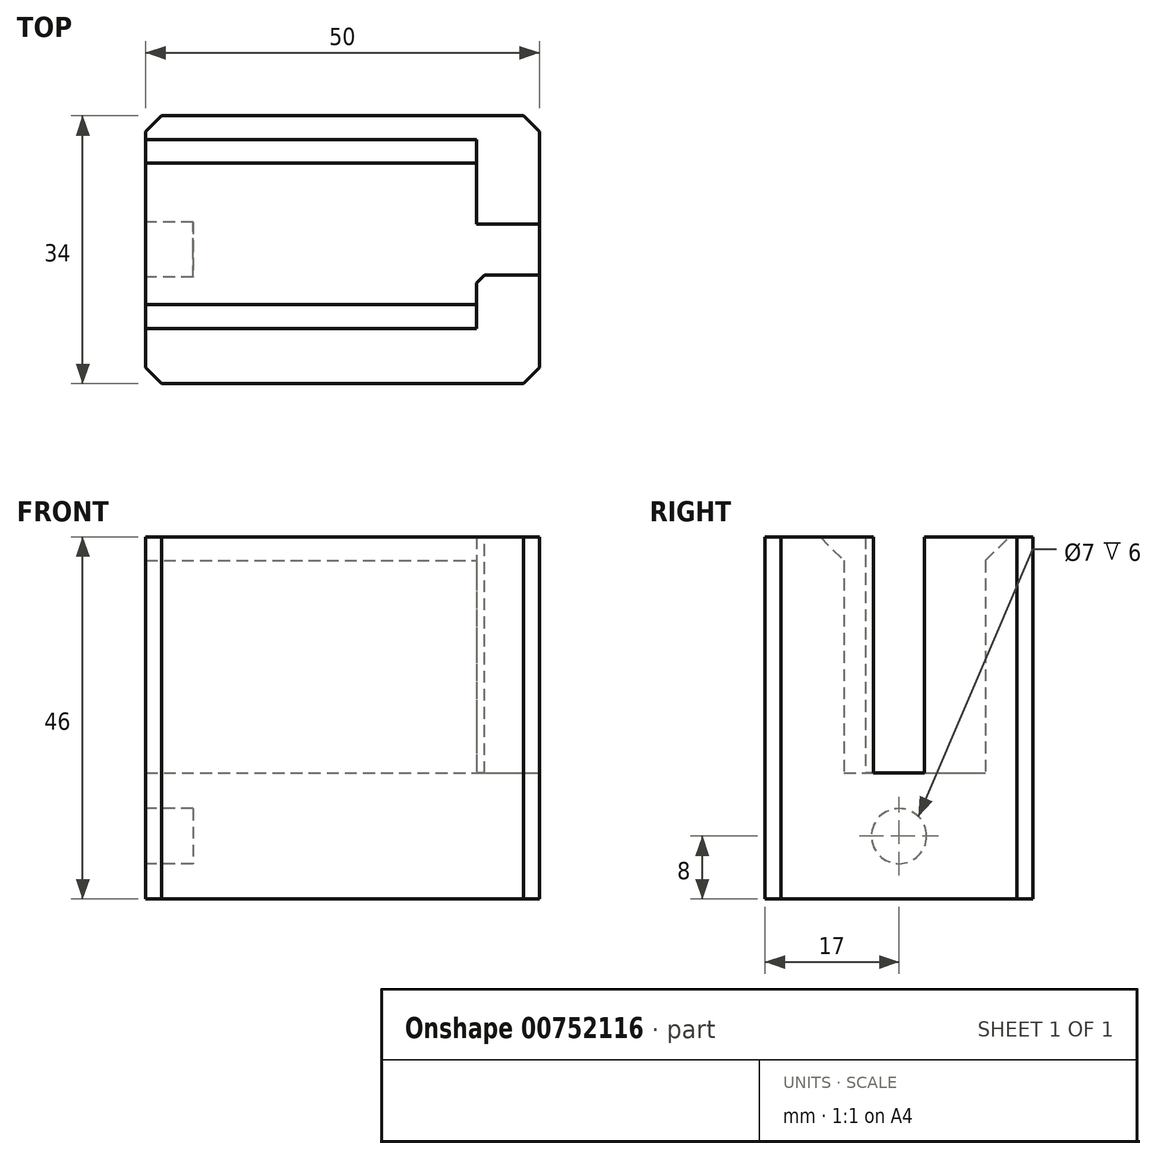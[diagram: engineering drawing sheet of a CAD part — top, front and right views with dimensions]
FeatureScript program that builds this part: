
annotation { "Feature Type Name" : "Feature", "Feature Type Description" : "" }
export const myFeature = defineFeature(function(context is Context, id is Id, definition is map)
    precondition{}
    {
        {
            var Q0;
            Q0=qCreatedBy(makeId("Front.planeOp"),FACE);
            var sketch = newSketch(context, id + "F0", { "sketchPlane" : qUnion([Q0])});
            skLineSegment(sketch, "E0.bottom", {"start": v(-25, 8) * mm, "end": v(-20, 8) * mm});
            skLineSegment(sketch, "E0.top", {"start": v(-25, -8) * mm, "end": v(25, -8) * mm});
            skLineSegment(sketch, "E0.left", {"start": v(-25, 8) * mm, "end": v(-25, -8) * mm});
            skLineSegment(sketch, "E0.right", {"start": v(25, 38) * mm, "end": v(25, -8) * mm});
            skPoint(sketch, "E0.middle", {"position": v(0, 0) * mm});
            skLineSegment(sketch, "E1.0", {"start": v(-20, 8) * mm, "end": v(-20, 8) * mm});
            skLineSegment(sketch, "E2.0", {"start": v(-20, 8) * mm, "end": v(17, 8) * mm});
            skLineSegment(sketch, "E3.0", {"start": v(17, 38) * mm, "end": v(17, 8) * mm});
            skPoint(sketch, "E4.orphan", {"position": v(25, 8) * mm});
            skLineSegment(sketch, "E5.trimOffspring", {"start": v(17, 38) * mm, "end": v(25, 38) * mm});
            skSolve(sketch);
        }
        {
            var Q0;
            Q0=qSketchRegion(id+"F0",true);
            extrude(context, id + "F1", {"entities" : qUnion([Q0]), "depth" : 34 * mm, "offsetDistance" : 25 * mm});
        }
        {
            var Q0;
            Q0=makeQuery(id+"F1.opExtrude","SWEPT_FACE",FACE,{"disambiguationData":[OSD([sQuery(id+"F0.wireOp",EDGE,"E0.right")])]});
            var sketch = newSketch(context, id + "F2", { "sketchPlane" : qUnion([Q0])});
            skLineSegment(sketch, "E6.bottom", {"start": v(-20.25, 38) * mm, "end": v(-13.75, 38) * mm});
            skLineSegment(sketch, "E6.top", {"start": v(-20.25, 8) * mm, "end": v(-13.75, 8) * mm});
            skLineSegment(sketch, "E6.left", {"start": v(-20.25, 38) * mm, "end": v(-20.25, 8) * mm});
            skLineSegment(sketch, "E6.right", {"start": v(-13.75, 38) * mm, "end": v(-13.75, 8) * mm});
            skSolve(sketch);
        }
        {
            var Q0;
            Q0=qSketchRegion(id+"F2",true);
            var Q1;
            Q1=makeQuery(id+"F1.opExtrude","SWEPT_FACE",FACE,{"disambiguationData":[OSD([sQuery(id+"F0.wireOp",EDGE,"E3.0")])]});
            extrude(context, id + "F3", {"entities" : qUnion([Q0]), "operationType" : NewBodyOperationType.REMOVE, "endBound" : BoundingType.UP_TO_SURFACE, "oppositeDirection" : true, "depth" : 25 * mm, "endBoundEntityFace" : qUnion([Q1]), "offsetDistance" : 25 * mm});
        }
        {
            var Q0;
            Q0=makeQuery(id+"F1.opExtrude","SWEPT_FACE",FACE,{"disambiguationData":[OSD([sQuery(id+"F0.wireOp",EDGE,"E0.left")])]});
            var sketch = newSketch(context, id + "F4", { "sketchPlane" : qUnion([Q0])});
            skCircle(sketch, "E7", {"center": v(17, 0) * mm, "radius": 3.5 * mm});
            skSolve(sketch);
        }
        {
            var Q0;
            Q0=qSketchRegion(id+"F4",true);
            extrude(context, id + "F5", {"entities" : qUnion([Q0]), "operationType" : NewBodyOperationType.REMOVE, "oppositeDirection" : true, "depth" : 6 * mm, "offsetDistance" : 25 * mm});
        }
        {
            var Q0;
            Q0=makeQuery(id+"F3.boolean.opBoolean","MERGE",FACE,{"derivedFrom":[makeQuery(id+"F1.opExtrude","SWEPT_FACE",FACE,{"disambiguationData":[OSD([sQuery(id+"F0.wireOp",EDGE,"E0.bottom"),sQuery(id+"F0.wireOp",EDGE,"E2.0")])]})],"fromTools":[makeQuery(id+"F3.opExtrude","SWEPT_FACE",FACE,{"disambiguationData":[OSD([sQuery(id+"F2.wireOp",EDGE,"E6.top")])]})]});
            var sketch = newSketch(context, id + "F6", { "sketchPlane" : qUnion([Q0])});
            skLineSegment(sketch, "E8.bottom", {"start": v(-25, -34) * mm, "end": v(17, -34) * mm});
            skLineSegment(sketch, "E8.top", {"start": v(-25, -24) * mm, "end": v(17, -24) * mm});
            skLineSegment(sketch, "E8.left", {"start": v(-25, -34) * mm, "end": v(-25, -24) * mm});
            skLineSegment(sketch, "E8.right", {"start": v(17, -34) * mm, "end": v(17, -24) * mm});
            skLineSegment(sketch, "E9.bottom", {"start": v(-25, 0) * mm, "end": v(17, 0) * mm});
            skLineSegment(sketch, "E9.top", {"start": v(-25, -6) * mm, "end": v(17, -6) * mm});
            skLineSegment(sketch, "E9.left", {"start": v(-25, 0) * mm, "end": v(-25, -6) * mm});
            skLineSegment(sketch, "E9.right", {"start": v(17, 0) * mm, "end": v(17, -6) * mm});
            skSolve(sketch);
        }
        {
            var Q0;
            Q0 = qSketchRegion(id + "F6", true);
            var Q1;
            {var subQ0=sQuery(id+"F0.wireOp",EDGE,"E5.trimOffspring");Q1=makeQuery(id+"F3.boolean.opBoolean","SPLIT",FACE,{"disambiguationData":[TD([makeQuery(id+"F3.opExtrude","SWEPT_FACE",FACE,{"disambiguationData":[OSD([sQuery(id+"F2.wireOp",EDGE,"E6.left")])]})])],"derivedFrom":makeQuery(id+"F1.opExtrude","SWEPT_FACE",FACE,{"disambiguationData":[OSD([subQ0])]})});}
            extrude(context, id + "F7", {"entities" : qUnion([Q0]), "operationType" : NewBodyOperationType.ADD, "endBound" : BoundingType.UP_TO_SURFACE, "depth" : 25 * mm, "endBoundEntityFace" : qUnion([Q1]), "offsetDistance" : 25 * mm});
        }
        {
            var Q0;
            Q0=makeQuery(id+"F7.opExtrude","CAP_EDGE",EDGE,{"disambiguationData":[OSD([sQuery(id+"F6.wireOp",EDGE,"E8.top")])],"isStart":false});
            var Q1;
            Q1=makeQuery(id+"F7.opExtrude","CAP_EDGE",EDGE,{"disambiguationData":[OSD([sQuery(id+"F6.wireOp",EDGE,"E9.top")])],"isStart":false});
            chamfer(context, id + "F8", {"entities" : qUnion([Q0, Q1]), "width" : 3 * mm, "tangentPropagation" : true});
        }
        {
            var Q0;
            Q0=makeQuery(id+"F1.opExtrude","CAP_EDGE",EDGE,{"disambiguationData":[OSD([sQuery(id+"F0.wireOp",EDGE,"E0.right")])],"isStart":false});
            var Q1;
            Q1=makeQuery(id+"F1.opExtrude","CAP_EDGE",EDGE,{"disambiguationData":[OSD([sQuery(id+"F0.wireOp",EDGE,"E0.right")])],"isStart":true});
            var Q2;
            Q2=makeQuery(id+"F7.boolean.opBoolean","MERGE",EDGE,{"derivedFrom":[makeQuery(id+"F1.opExtrude","CAP_EDGE",EDGE,{"disambiguationData":[OSD([sQuery(id+"F0.wireOp",EDGE,"E0.left")])],"isStart":false}),makeQuery(id+"F7.opExtrude","SWEPT_EDGE",EDGE,{"disambiguationData":[OSD([sQuery(id+"F6.wireOp",EDGE,"E8.bottom"),sQuery(id+"F6.wireOp",EDGE,"E8.left")])]})]});
            var Q3;
            Q3=makeQuery(id+"F7.boolean.opBoolean","MERGE",EDGE,{"derivedFrom":[makeQuery(id+"F1.opExtrude","CAP_EDGE",EDGE,{"disambiguationData":[OSD([sQuery(id+"F0.wireOp",EDGE,"E0.left")])],"isStart":true}),makeQuery(id+"F7.opExtrude","SWEPT_EDGE",EDGE,{"disambiguationData":[OSD([sQuery(id+"F6.wireOp",EDGE,"E9.bottom"),sQuery(id+"F6.wireOp",EDGE,"E9.left")])]})]});
            chamfer(context, id + "F9", {"entities" : qUnion([Q0, Q1, Q2, Q3]), "width" : 2 * mm, "tangentPropagation" : true});
        }
        {
            var Q0;
            Q0=makeQuery(id+"F3.boolean.opBoolean","COPY",EDGE,{"derivedFrom":makeQuery(id+"F3.opExtrude","CAP_EDGE",EDGE,{"disambiguationData":[OSD([sQuery(id+"F2.wireOp",EDGE,"E6.right")])],"isStart":false})});
            var Q1;
            Q1=makeQuery(id+"F3.boolean.opBoolean","COPY",EDGE,{"derivedFrom":makeQuery(id+"F3.opExtrude","CAP_EDGE",EDGE,{"disambiguationData":[OSD([sQuery(id+"F2.wireOp",EDGE,"E6.left")])],"isStart":false})});
            var Q2;
            Q2=makeQuery(id+"F3.boolean.opBoolean","COPY",EDGE,{"derivedFrom":makeQuery(id+"F3.opExtrude","CAP_EDGE",EDGE,{"disambiguationData":[OSD([sQuery(id+"F2.wireOp",EDGE,"E6.right")])],"isStart":true})});
            var Q3;
            Q3=makeQuery(id+"F3.boolean.opBoolean","COPY",EDGE,{"derivedFrom":makeQuery(id+"F3.opExtrude","CAP_EDGE",EDGE,{"disambiguationData":[OSD([sQuery(id+"F2.wireOp",EDGE,"E6.left")])],"isStart":true})});
            chamfer(context, id + "F10", {"entities" : qUnion([Q0, Q1, Q2, Q3]), "width" : 1 * mm, "tangentPropagation" : true});
        }
    });
